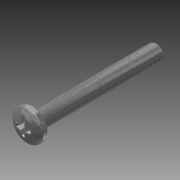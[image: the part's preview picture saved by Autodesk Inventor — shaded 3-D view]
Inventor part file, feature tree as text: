
AUTODESK INVENTOR PART (.ipt)
format: ipt  version: 2014 SP1 (Build 180222100, 222)  size: 1,116,672 bytes
history: native  units: in
note: dims shown in document units (in); Inventor stores cm internally (conversion verified against a paired STEP export)
features: fillet x1, other x1, imported_body x1
ambient origin geometry x8: Origin, YZ Plane, XZ Plane, XY Plane, X Axis, Y Axis, Z Axis, Center Point
bodies: Body1 (feature_tree)
feature tree (3):
  fillet  "Fillet1"  [1 undecoded]
  other  "91735A8411"
  imported_body  "Base1"
note: 1 required parameter value undecoded (feature->parameter linkage not recoverable at this tier; creation-order binding heuristic only, values carry confidence <= 0.55)
